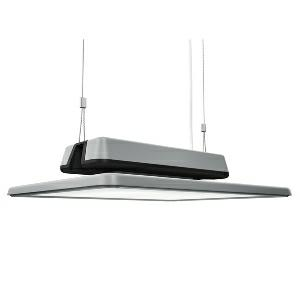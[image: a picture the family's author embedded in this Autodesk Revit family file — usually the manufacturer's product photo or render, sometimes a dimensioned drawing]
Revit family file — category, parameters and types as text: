
# Revit family: acaneo_-_hial_37000_840_n_dali_00804837_7c4a
name_source: partatom
category: Lighting Fixtures
units: mm (PartAtom-declared; Revit-internal decimal feet)

## family parameters
Cut with Voids When Loaded = No
Host = Face
Light Source = No
Part Type = Normal
Room Calculation Point = No
Round Connector Dimension = Use Diameter
Shared = No

## types (1)
- ACANEO - HIAL 37000/840/N/DALI (1 x LED, 40000 lm, 4000K)
    Apparent Load = 262 VA
    Approval mark = CE
    CIE Flux Codes = 84 97 100 100 100
    Color Rendering = 80-89
    Color Temperature = 4000K
    Control Gear = Electronic ballast
    Default Elevation = 1800 mm
    Description = HIAL 37000/840/N/DALI|High bay luminaire|light source: LED|work equipment: Adjustable electronic ballast, digital DALI|connected load: 220-240 V, 50/60 Hz|Power consumption: approx. 262 W|power factor: approx. 0,981|luminous flux: 40000 lm|luminous efficacy: 152 lm/W|colour temperature: Cold white, ca. 4000 K|color rendering index (CRI): >= 80|chromaticity tolerance:  3 SDCM|System of protection: IP 65|class of protection: I|technology: Continuously dimmable|luminaire body|material: Aluminium|surface: Powder coatet|colour: White aluminium|lamp cover: Acrylic (PMMA), Clear|weight (net): approx. 10.8 kg|mains lead: Built-in plug RST 20i5 Einbau|Fastening: Available separately|Accessory: Junction box (RST 20i5)|minimum ambient temperature: -30 ░C|maximum ambient temperature: 50 ░C|glare control: Optics|unified glare rating(4H 8H): <=  22|
    Frequency = 50 Hz, 60 Hz
    Height = 125 mm
    Lamp = 1 x LED
    Lamp Light Flux = 40000 lm
    Lamp count = 1
    Length = 585 mm
    Luminous efficacy = 153 lm/W
    Manufacturer = Waldmann
    ModVariant = No
    Model = 00804837
    Mounting Place = Ceiling
    Mounting Type = Pendant
    Number of Poles = 1
    OnlyDefault = Yes
    Power Factor = 1
    Product Name = ACANEO - HIAL 37000/840/N/DALI
    Product group = High bay luminaire (industry)
    ProductGroupID = 901
    Protection Class = Protection class I
    Protection Degree = IP 65
    RLX_Detail_Level = 1
    RLX_Emergency_Light_Flux = 0 lm
    RLX_Emergency_Type = 0
    RLX_Emergency_Type_DB = No
    RlxData = <blob elided: 29921 chars, md5=69d97270>
    Socket = socket
    Standby Power = 0 W
    System Light Flux = 40000 lm
    System Power = 262 W
    Type Comments = Product without accessories
    Type Image = acaneo-hial.jpg
    URL = http://relux.com
    VarID = ---
    Voltage = 230 V
    Voltage Range = 110-120 V, 220-240 V
    Weight = 0.00 kg
    Width = 480 mm

## geometry (parser evidence)
native form markers: Blend x4, Sweep x11
no freeform markers — native parametric forms only
